# Revit family: Lighting Fixture_Sylvania_Expospot 50 Fixed_Ceiling Recessed1
name_source: partatom
category: Lighting Fixtures
revit_build: Autodesk Revit 2016 (Build: 20161004_0715(x64)
units: mm (PartAtom-declared; Revit-internal decimal feet)

## family parameters
Cut with Voids When Loaded = No
Host = Face
Light Source = Yes
OmniClass Number = 23.80.70.11.17
OmniClass Title = Specialized Lighting by Location or Use
Part Type = Normal
Room Calculation Point = No
Round Connector Dimension = Use Diameter
Shared = No

## types (12) — shared parameters
Apparent Load = 13 VA
Assembly Code = D5020200
Average Life = 50 000h
Body Material = Aluminum_Sylvania_Expospot_White
Color Filter = 16777215
Colour Variation Initial = 3SDCM
Control Gear Mounting = Remote
Control Gear Required = No
Control Gear Type = Electronic
Cooling Big Axis = 35 mm
Cooling Material = Plastic_Sylvania_Expospot_Black
Cooling Small Axis = 24.5 mm  [stored 0.0803806 ft]
Cutout Diameter = 85 mm
Description = Specifically designed for Retail and Display applications. I.e. Supermarkets, Fashion Retail, Department stores. Build around a 50mm reflector and lens combination.
Diameter = 95 mm
Dimmable = N
Dimming Lamp Color Temperature Shift = <None>
Drive Current = 300mA
Electrical Protection = Class II
Emit Shape Visible in Rendering = No
Emit from Circle Diameter = 70 mm
Glow Wire Test = 850 °C
Height = 103 mm  [stored 0.337927 ft]
IK Rating = IK02
IP Rating = IP20
Inrush Current = 17 A
Inrush Duration = 199µs
LOR = 100%
Lamp = LED
Lamp Power Factor = 0.83
Manufacturer = Feilo Sylvania
Max. Luminaires per 10A B Breaker = 23
Max. Luminaires per 10A C Breaker = 38
Max. Luminaires per 13A B Breaker = 30
Max. Luminaires per 13A C Breaker = 50
Max. Luminaires per 16A B Breaker = 37
Max. Luminaires per 16A C Breaker = 61
Max. Luminaires per 20A B Breaker = 47
Max. Luminaires per 20A C Breaker = 78
Nominal Frequency = 50/60Hz
Photobiological Risk Group = RG1
Product Family = EXPOSPOT 50 FIXED
Product Page URL = http://www.sylvania-lighting.com
Radius = 47.5 mm
Reflector Material = Aluminum_Sylvania_Expospot_Polished
Tilt Angle = -90°
Total Power Consumption = 13 W
URL = http://www.sylvania-lighting.com
Voltage = 240 V
Voltage Comments = 220-240V~
Weight = 1 kg
zero-valued in all types: Default Elevation

## per-type parameters (varying)
| type | Beam Angle | CRI | Diffuser Material | Photometric Web File | Product Code |
| EXPOSPOT 50 FIX 90 4K WB WHT | 41° | 90Ra | Arcylic_Sylvania_Expospot_4000K | 0060212.ies | 0060212 |
| EXPOSPOT 50 FIX 90 4K MB WHT | 33° | 90Ra | Arcylic_Sylvania_Expospot_4000K | 0060211.ies | 0060211 |
| EXPOSPOT 50 FIX 90 4K NB WHT | 22° | 90Ra | Arcylic_Sylvania_Expospot_4000K | 0060210.ies | 0060210 |
| EXPOSPOT 50 FIX 90 3K WB WHT | 45° | 90Ra | Arcylic_Sylvania_Expospot_3000K | 0060209.ies | 0060209 |
| EXPOSPOT 50 FIX 90 3K MB WHT | 33° | 90Ra | Arcylic_Sylvania_Expospot_3000K | 0060208.ies | 0060208 |
| EXPOSPOT 50 FIX 90 3K NB WHT | 22° | 90Ra | Arcylic_Sylvania_Expospot_3000K | 0060207.ies | 0060207 |
| EXPOSPOT 50 FIX 80 4K WB WHT | 50° | 80Ra | Arcylic_Sylvania_Expospot_4000K | 0060206.ies | 0060206 |
| EXPOSPOT 50 FIX 80 4K MB WHT | 32° | 80Ra | Arcylic_Sylvania_Expospot_4000K | 0060205.ies | 0060205 |
| EXPOSPOT 50 FIX 80 4K NB WHT | 22° | 80Ra | Arcylic_Sylvania_Expospot_4000K | 0060204.ies | 0060204 |
| EXPOSPOT 50 FIX 80 3K WB WHT | 51° | 80Ra | Arcylic_Sylvania_Expospot_3000K | 0060203.ies | 0060203 |
| EXPOSPOT 50 FIX 80 3K MB WHT | 35° | 80Ra | Arcylic_Sylvania_Expospot_3000K | 0060202.ies | 0060202 |
| EXPOSPOT 50 FIX 80 3K NB WHT | 22° | 80Ra | Arcylic_Sylvania_Expospot_3000K | 0060201.ies | 0060201 |

note: column(s) folded — value = type name in every type: Model

note: [stored X ft] marks values corroborated as IEEE doubles in the binary element streams (Revit-internal decimal feet)

## geometry (parser evidence)
native form markers: Sweep x2
no freeform markers — native parametric forms only
